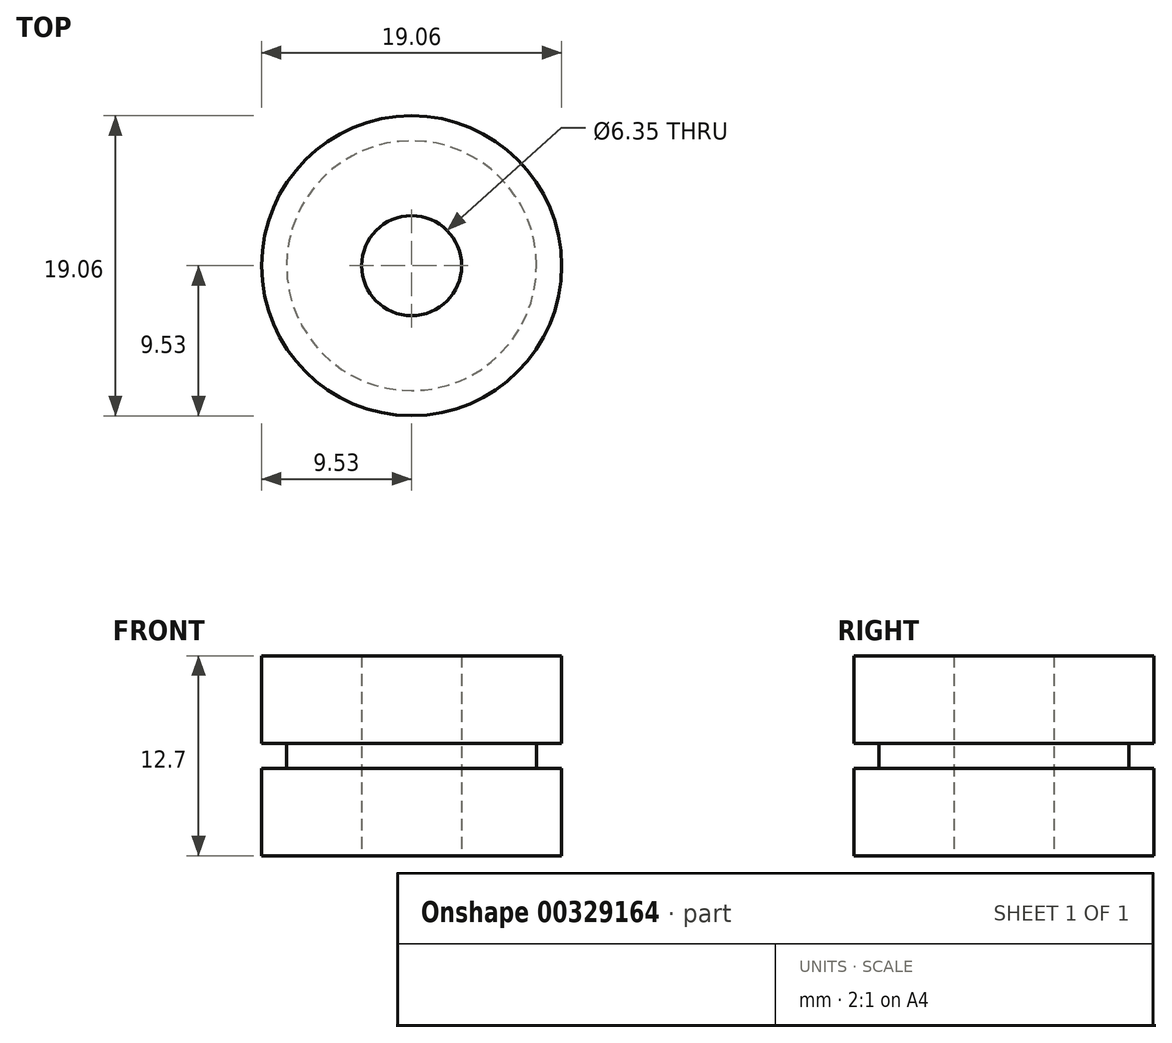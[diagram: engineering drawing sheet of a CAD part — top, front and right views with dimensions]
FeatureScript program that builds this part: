
annotation { "Feature Type Name" : "Feature", "Feature Type Description" : "" }
export const myFeature = defineFeature(function(context is Context, id is Id, definition is map)
    precondition{}
    {
        {
            var Q0;
            Q0=qCreatedBy(makeId("Front.planeOp"),FACE);
            var sketch = newSketch(context, id + "F0", { "sketchPlane" : qUnion([Q0])});
            skLineSegment(sketch, "E0", {"start": v(-3.18, -5.56) * mm, "end": v(-3.18, 7.14) * mm});
            skLineSegment(sketch, "E1", {"start": v(-3.18, 7.14) * mm, "end": v(-9.53, 7.14) * mm});
            skLineSegment(sketch, "E2", {"start": v(-9.53, 7.14) * mm, "end": v(-9.53, 1.59) * mm});
            skLineSegment(sketch, "E3", {"start": v(-9.53, 1.59) * mm, "end": v(-7.94, 1.59) * mm});
            skLineSegment(sketch, "E4", {"start": v(-7.94, 1.59) * mm, "end": v(-7.94, 0) * mm});
            skLineSegment(sketch, "E5", {"start": v(-7.94, 0) * mm, "end": v(-9.53, 0) * mm});
            skLineSegment(sketch, "E6", {"start": v(-9.53, 0) * mm, "end": v(-9.53, -5.56) * mm});
            skLineSegment(sketch, "E7", {"start": v(-9.52, -5.56) * mm, "end": v(-3.17, -5.56) * mm});
            skLineSegment(sketch, "E8", {"start": v(0, -25.4) * mm, "end": v(0, 25.4) * mm, "construction": true});
            skSolve(sketch);
        }
        {
            var Q0;
            Q0=makeQuery(id+"F0.imprint","IMPRINT",FACE,{"disambiguationData":[TD([[makeQuery(id+"F0.imprint","IMPRINT",EDGE,{"derivedFrom":sQuery(id+"F0.wireOp",EDGE,"E0")}),1.0]])]});
            var Q1;
            Q1=sQuery(id+"F0.wireOp",EDGE,"E8");
            revolve(context, id + "F1", {"entities" : qUnion([Q0]), "axis" : qUnion([Q1]), "revolveType" : RevolveType.FULL});
        }
    });
